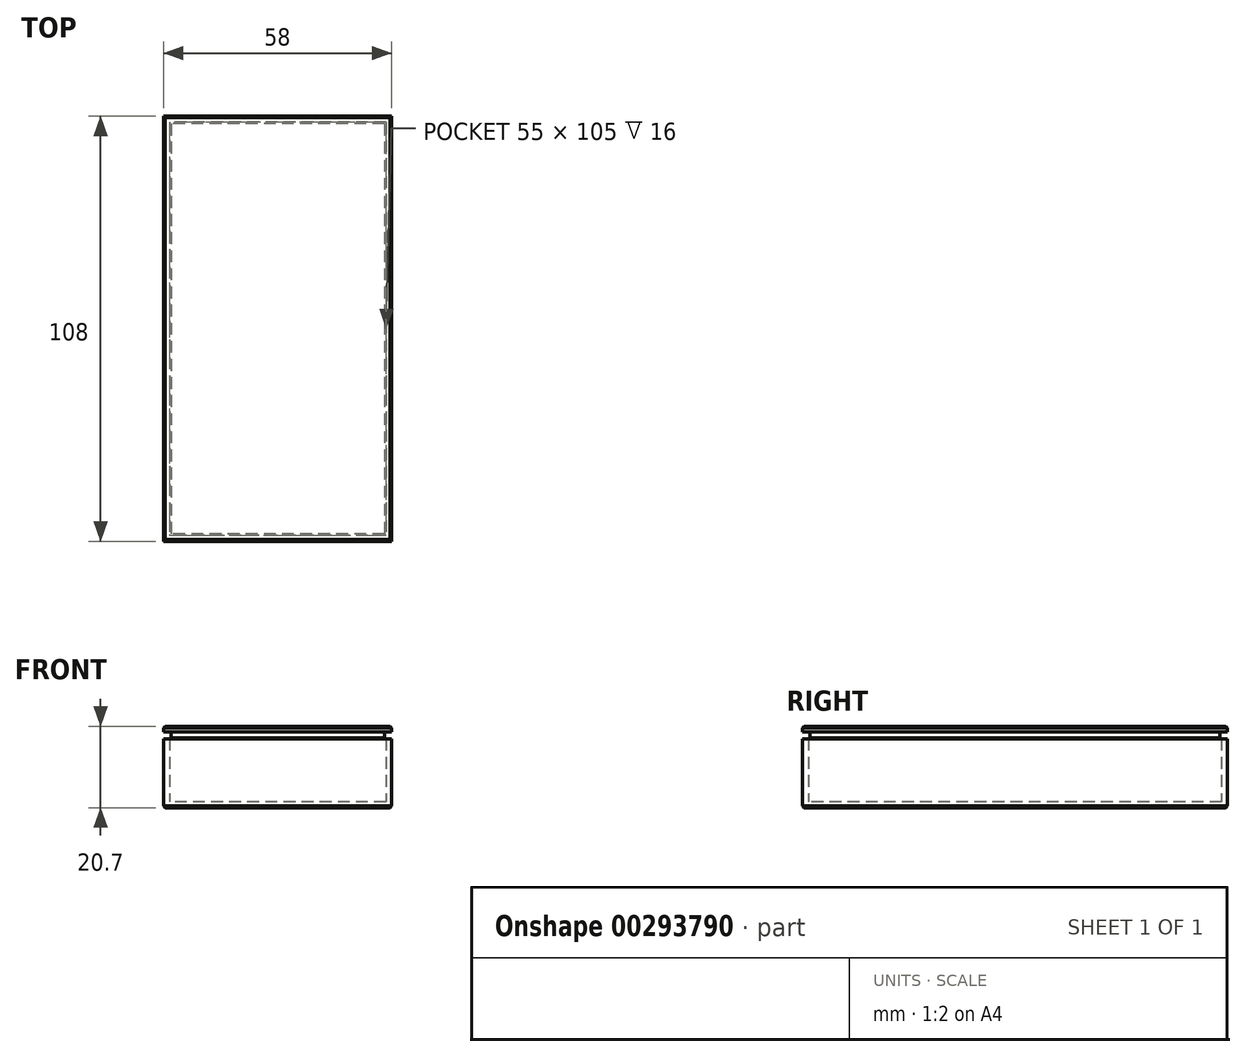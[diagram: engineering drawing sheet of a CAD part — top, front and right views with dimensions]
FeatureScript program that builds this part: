
annotation { "Feature Type Name" : "Feature", "Feature Type Description" : "" }
export const myFeature = defineFeature(function(context is Context, id is Id, definition is map)
    precondition{}
    {
        {
            var Q0;
            Q0=qCreatedBy(makeId("Top.planeOp"),FACE);
            var sketch = newSketch(context, id + "F0", { "sketchPlane" : qUnion([Q0])});
            skLineSegment(sketch, "E0.bottom", {"start": v(29, -54) * mm, "end": v(-29, -54) * mm});
            skLineSegment(sketch, "E0.top", {"start": v(29, 54) * mm, "end": v(-29, 54) * mm});
            skLineSegment(sketch, "E0.left", {"start": v(29, -54) * mm, "end": v(29, 54) * mm});
            skLineSegment(sketch, "E0.right", {"start": v(-29, -54) * mm, "end": v(-29, 54) * mm});
            skPoint(sketch, "E0.middle", {"position": v(0, 0) * mm});
            skSolve(sketch);
        }
        {
            var Q0;
            Q0 = qSketchRegion(id + "F0", true);
            extrude(context, id + "F1", {"entities" : qUnion([Q0]), "depth" : 1.5 * mm, "offsetDistance" : 25 * mm});
        }
        {
            var Q0;
            Q0=makeQuery(id+"F1.opExtrude","CAP_FACE",FACE,{"disambiguationData":[OSD([sQuery(id+"F0.wireOp",EDGE,"E0.bottom"),sQuery(id+"F0.wireOp",EDGE,"E0.top"),sQuery(id+"F0.wireOp",EDGE,"E0.left"),sQuery(id+"F0.wireOp",EDGE,"E0.right")])],"isStart":false});
            var sketch = newSketch(context, id + "F2", { "sketchPlane" : qUnion([Q0])});
            skLineSegment(sketch, "E1.bottom", {"start": v(-29, 54) * mm, "end": v(29, 54) * mm});
            skLineSegment(sketch, "E1.top", {"start": v(-29, -54) * mm, "end": v(29, -54) * mm});
            skLineSegment(sketch, "E1.left", {"start": v(-29, 54) * mm, "end": v(-29, -54) * mm});
            skLineSegment(sketch, "E1.right", {"start": v(29, 54) * mm, "end": v(29, -54) * mm});
            skLineSegment(sketch, "E2.bottom", {"start": v(27.5, 52.5) * mm, "end": v(-27.5, 52.5) * mm});
            skLineSegment(sketch, "E2.top", {"start": v(27.5, -52.5) * mm, "end": v(-27.5, -52.5) * mm});
            skLineSegment(sketch, "E2.left", {"start": v(27.5, 52.5) * mm, "end": v(27.5, -52.5) * mm});
            skLineSegment(sketch, "E2.right", {"start": v(-27.5, 52.5) * mm, "end": v(-27.5, -52.5) * mm});
            skPoint(sketch, "E2.middle", {"position": v(0, 0) * mm});
            skSolve(sketch);
        }
        {
            var Q0;
            Q0 = qSketchRegion(id + "F2", true);
            extrude(context, id + "F3", {"entities" : qUnion([Q0]), "operationType" : NewBodyOperationType.ADD, "depth" : 16 * mm, "offsetDistance" : 25 * mm});
        }
        {
            var Q0;
            Q0=makeQuery(id+"F3.opExtrude","CAP_FACE",FACE,{"disambiguationData":[OSD([sQuery(id+"F2.wireOp",EDGE,"E1.bottom"),sQuery(id+"F2.wireOp",EDGE,"E1.top"),sQuery(id+"F2.wireOp",EDGE,"E1.left"),sQuery(id+"F2.wireOp",EDGE,"E1.right"),sQuery(id+"F2.wireOp",EDGE,"E2.bottom"),sQuery(id+"F2.wireOp",EDGE,"E2.top"),sQuery(id+"F2.wireOp",EDGE,"E2.left"),sQuery(id+"F2.wireOp",EDGE,"E2.right")])],"isStart":false});
            cPlane(context, id + "F4", {"entities" : qUnion([Q0]), "cplaneType" : CPlaneType.OFFSET, "offset" : .2 * mm, "width" : 150 * mm, "height" : 150 * mm});
        }
        {
            var Q0;
            Q0=qCreatedBy(id+"F4.planeOp",FACE);
            var sketch = newSketch(context, id + "F5", { "sketchPlane" : qUnion([Q0])});
            skLineSegment(sketch, "E3.bottom", {"start": v(27.1, 52.1) * mm, "end": v(-27.1, 52.1) * mm});
            skLineSegment(sketch, "E3.top", {"start": v(27.1, -52.1) * mm, "end": v(-27.1, -52.1) * mm});
            skLineSegment(sketch, "E3.left", {"start": v(27.1, 52.1) * mm, "end": v(27.1, -52.1) * mm});
            skLineSegment(sketch, "E3.right", {"start": v(-27.1, 52.1) * mm, "end": v(-27.1, -52.1) * mm});
            skPoint(sketch, "E3.middle", {"position": v(0, 0) * mm});
            skSolve(sketch);
        }
        {
            var Q0;
            Q0 = qSketchRegion(id + "F5", true);
            extrude(context, id + "F6", {"entities" : qUnion([Q0]), "depth" : 1.5 * mm, "offsetDistance" : 25 * mm});
        }
        {
            var Q0;
            Q0=makeQuery(id+"F6.opExtrude","CAP_FACE",FACE,{"disambiguationData":[OSD([sQuery(id+"F5.wireOp",EDGE,"E3.bottom"),sQuery(id+"F5.wireOp",EDGE,"E3.top"),sQuery(id+"F5.wireOp",EDGE,"E3.left"),sQuery(id+"F5.wireOp",EDGE,"E3.right")])],"isStart":false});
            var sketch = newSketch(context, id + "F7", { "sketchPlane" : qUnion([Q0])});
            skLineSegment(sketch, "E4.bottom", {"start": v(29, -54) * mm, "end": v(-29, -54) * mm});
            skLineSegment(sketch, "E4.top", {"start": v(29, 54) * mm, "end": v(-29, 54) * mm});
            skLineSegment(sketch, "E4.left", {"start": v(29, -54) * mm, "end": v(29, 54) * mm});
            skLineSegment(sketch, "E4.right", {"start": v(-29, -54) * mm, "end": v(-29, 54) * mm});
            skPoint(sketch, "E4.middle", {"position": v(0, 0) * mm});
            skSolve(sketch);
        }
        {
            var Q0;
            Q0 = qSketchRegion(id + "F7", true);
            extrude(context, id + "F8", {"entities" : qUnion([Q0]), "operationType" : NewBodyOperationType.ADD, "depth" : 1.5 * mm, "offsetDistance" : 25 * mm});
        }
        {
            var Q0;
            Q0=makeQuery(id+"F8.opExtrude","CAP_FACE",FACE,{"disambiguationData":[OSD([sQuery(id+"F7.wireOp",EDGE,"E4.bottom"),sQuery(id+"F7.wireOp",EDGE,"E4.top"),sQuery(id+"F7.wireOp",EDGE,"E4.left"),sQuery(id+"F7.wireOp",EDGE,"E4.right")])],"isStart":false});
            var Q1;
            Q1=makeQuery(id+"F1.opExtrude","CAP_FACE",FACE,{"disambiguationData":[OSD([sQuery(id+"F0.wireOp",EDGE,"E0.bottom"),sQuery(id+"F0.wireOp",EDGE,"E0.top"),sQuery(id+"F0.wireOp",EDGE,"E0.left"),sQuery(id+"F0.wireOp",EDGE,"E0.right")])],"isStart":true});
            chamfer(context, id + "F9", {"entities" : qUnion([Q0, Q1]), "width" : .4 * mm, "tangentPropagation" : true});
        }
    });
